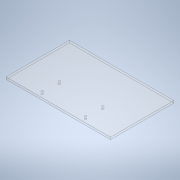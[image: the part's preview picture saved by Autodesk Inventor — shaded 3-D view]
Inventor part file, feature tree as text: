
AUTODESK INVENTOR PART (.ipt)
format: ipt  version: 2022 (Build 260153000, 153)  size: 114,688 bytes
history: native  units: mm
features: extrude x2, sketch x2
ambient origin geometry x8: Origin, YZ Plane, XZ Plane, XY Plane, X Axis, Y Axis, Z Axis, Center Point
bodies: Solid1 (feature_tree)
feature tree (4):
  extrude  "Lid"  Depth=3.0mm
  extrude  "M3_Mount_Holes"  Depth=23.0mm
  sketch  "Sketch1"  dims[d0=140.0mm d1=85.0mm d2=3.0mm]
  sketch  "Sketch2"  dims[d3=0.0mm d4=23.0mm d5=58.0mm d6=12.0mm d7=2.8mm d9=0.0mm d10=0.0mm]
